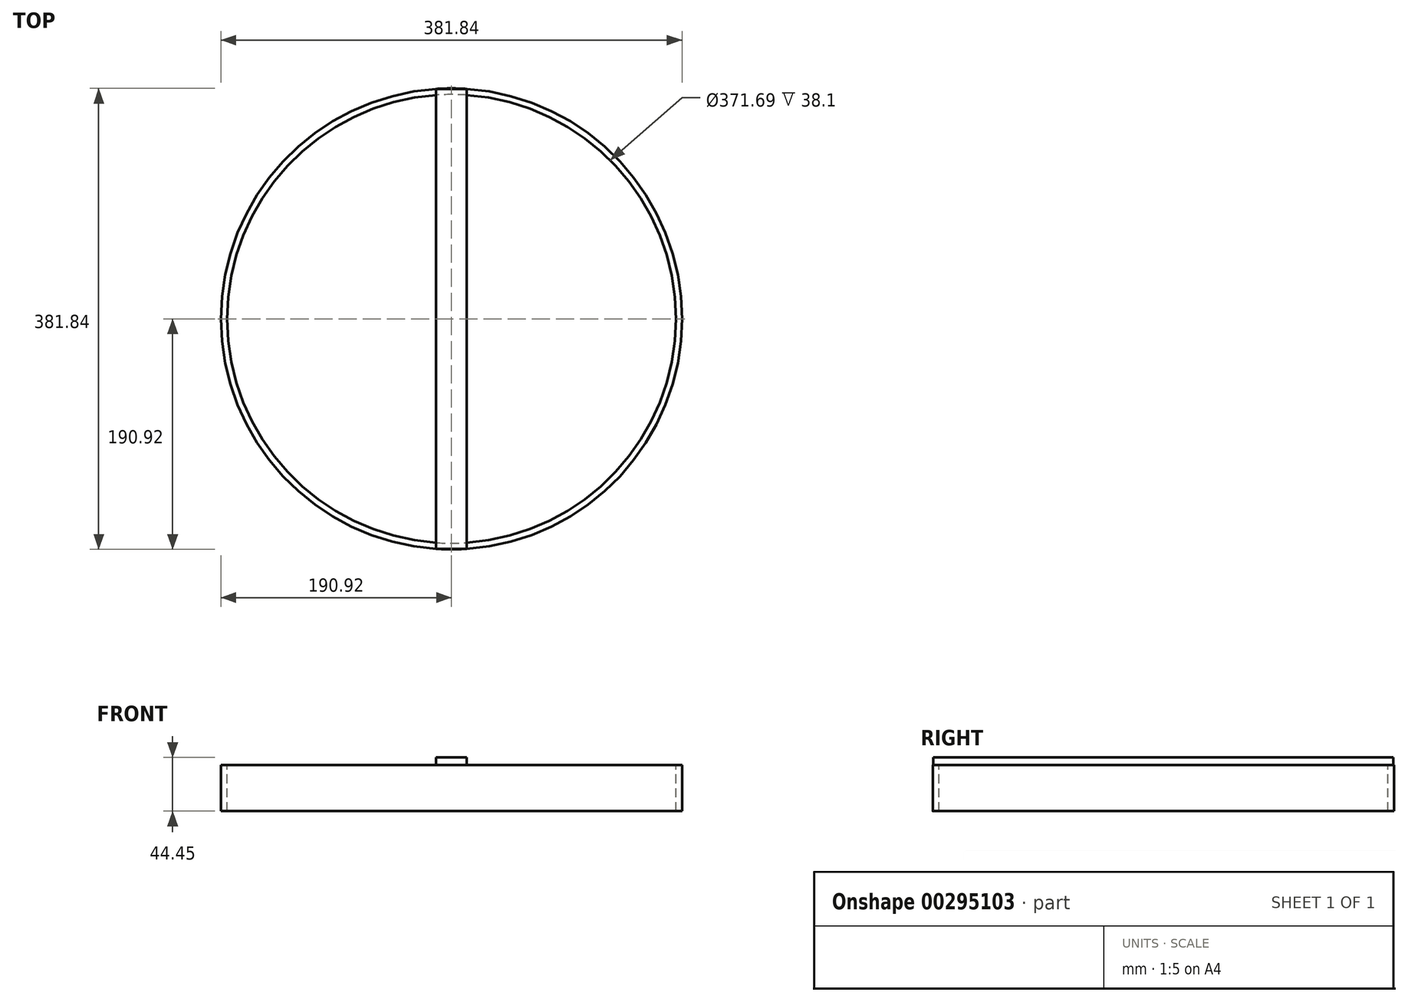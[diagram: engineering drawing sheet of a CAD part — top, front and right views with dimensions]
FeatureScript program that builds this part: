
annotation { "Feature Type Name" : "Feature", "Feature Type Description" : "" }
export const myFeature = defineFeature(function(context is Context, id is Id, definition is map)
    precondition{}
    {
        {
            var Q0;
            Q0=qCreatedBy(makeId("Top.planeOp"),FACE);
            var sketch = newSketch(context, id + "F0", { "sketchPlane" : qUnion([Q0])});
            skLineSegment(sketch, "E0.bottom", {"start": v(12.7, -190.5) * mm, "end": v(-12.7, -190.5) * mm});
            skLineSegment(sketch, "E0.top", {"start": v(12.7, 190.5) * mm, "end": v(-12.7, 190.5) * mm});
            skLineSegment(sketch, "E0.left", {"start": v(12.7, -190.5) * mm, "end": v(12.7, 190.5) * mm});
            skLineSegment(sketch, "E0.right", {"start": v(-12.7, -190.5) * mm, "end": v(-12.7, 190.5) * mm});
            skSolve(sketch);
        }
        {
            var Q0;
            Q0 = qSketchRegion(id + "F0", true);
            extrude(context, id + "F1", {"entities" : qUnion([Q0]), "depth" : 6.35 * mm});
        }
        {
            var Q0;
            Q0=makeQuery(id+"F1.opExtrude","CAP_FACE",FACE,{"disambiguationData":[OSD([sQuery(id+"F0.wireOp",EDGE,"E0.bottom"),sQuery(id+"F0.wireOp",EDGE,"E0.top"),sQuery(id+"F0.wireOp",EDGE,"E0.left"),sQuery(id+"F0.wireOp",EDGE,"E0.right")])],"isStart":true});
            var sketch = newSketch(context, id + "F2", { "sketchPlane" : qUnion([Q0])});
            skCircle(sketch, "E1", {"center": v(0, 0) * mm, "radius": 190.92 * mm});
            skCircle(sketch, "E2.0", {"center": v(0, 0) * mm, "radius": 185.84 * mm});
            skSolve(sketch);
        }
        {
            var Q0;
            Q0 = qSketchRegion(id + "F2", true);
            extrude(context, id + "F3", {"entities" : qUnion([Q0]), "operationType" : NewBodyOperationType.ADD, "depth" : 38.1 * mm});
        }
    });
